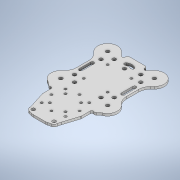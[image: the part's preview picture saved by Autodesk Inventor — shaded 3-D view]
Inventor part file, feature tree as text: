
AUTODESK INVENTOR PART (.ipt)
format: ipt  version: 2020 (Build 240168000, 168)  size: 273,920 bytes
history: native  units: mm
features: extrude x2, sketch x2
ambient origin geometry x8: Origin, YZ Plane, XZ Plane, XY Plane, X Axis, Y Axis, Z Axis, Center Point
bodies: Solid1 (feature_tree)
feature tree (4):
  extrude  "Extrusion1"  Depth=3.0mm TaperAngle=0.0deg
  extrude  "Extrusion2"  [1 undecoded]
  sketch  "Sketch1"  dims[d0=3.0mm d1=0.0mm d2=3.0mm d3=0.0mm]
  sketch  "Sketch2"
note: 1 required parameter value undecoded (feature->parameter linkage not recoverable at this tier; creation-order binding heuristic only, values carry confidence <= 0.55)
